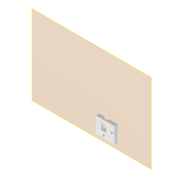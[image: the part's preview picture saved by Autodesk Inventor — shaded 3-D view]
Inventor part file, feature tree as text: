
AUTODESK INVENTOR PART (.ipt)
format: ipt  version: 2022 (Build 260153000, 153)  size: 137,216 bytes
history: native  units: mm
features: other x3, extrude x2, sketch x2, plane x1, chamfer x1, reference x1, projected_geometry x1
ambient origin geometry x8: Origin, YZ Plane, XZ Plane, XY Plane, X Axis, Y Axis, Z Axis, Center Point
bodies: Volumenkörper1 (feature_tree)
feature tree (11):
  plane  "Arbeitsebene1"
  extrude  "Extrusion1"  Depth=3.0mm
  extrude  "Extrusion2"  Depth=4.0mm TaperAngle=0.0deg
  chamfer  "Fase1"  Distance=2.0mm
  sketch  "Skizze1"  dims[d0=0.5mm d1=3.0mm]
  reference  "Referenz1"
  sketch  "Skizze2"  dims[d2=3.0mm d3=4.0mm d4=0.0mm d5=2.0mm d6=0.0mm d7=1.8mm d8=2.0mm d9=45.0deg]
  projected_geometry  "Projizierte Kontur1"
  other  "<userpath>\Documents\GitHub\Guinardia\INVENTOR\Assembly_Guinardia_V1.iam"
  other  "Assembly_Guinardia_V1.iam"
  other  "10_Wellplate_base_v1:1"
